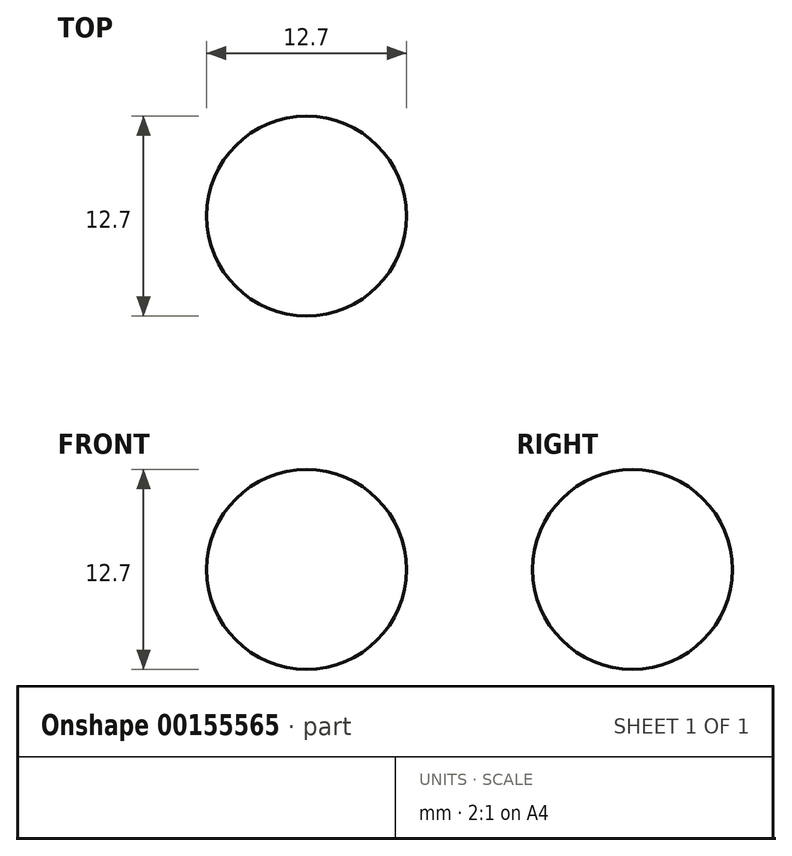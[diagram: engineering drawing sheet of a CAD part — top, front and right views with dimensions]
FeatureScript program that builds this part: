
annotation { "Feature Type Name" : "Feature", "Feature Type Description" : "" }
export const myFeature = defineFeature(function(context is Context, id is Id, definition is map)
    precondition{}
    {
        {
            var Q0;
            Q0=qCreatedBy(makeId("Top.planeOp"),FACE);
            var sketch = newSketch(context, id + "F0", { "sketchPlane" : qUnion([Q0])});
            skArc(sketch, "E0", {"start": v(0, 0) * mm, "mid": v(6.35, 6.35) * mm, "end": v(0, 12.7) * mm});
            skSolve(sketch);
        }
        {
            var Q0;
            Q0=qCreatedBy(makeId("Top.planeOp"),FACE);
            var sketch = newSketch(context, id + "F1", { "sketchPlane" : qUnion([Q0])});
            skLineSegment(sketch, "E1", {"start": v(0, 12.7) * mm, "end": v(0, 0) * mm});
            skSolve(sketch);
        }
        {
            var Q0;
            Q0=sQuery(id+"F0.wireOp",EDGE,"E0");
            var Q1;
            Q1=sQuery(id+"F1.wireOp",EDGE,"E1");
            revolve(context, id + "F2", {"bodyType" : ToolBodyType.SURFACE, "surfaceEntities" : qUnion([Q0]), "axis" : qUnion([Q1]), "revolveType" : RevolveType.FULL});
        }
    });
